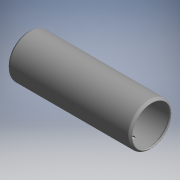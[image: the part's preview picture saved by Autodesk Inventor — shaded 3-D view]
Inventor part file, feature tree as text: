
AUTODESK INVENTOR PART (.ipt)
format: ipt  version: 2017.3 (Build 213256000, 256)  size: 147,456 bytes
history: native  units: mm (DEFAULTED — no unit token found)
features: other x42, sketch x2, revolve x1, extrude x1
ambient origin geometry x8: Origin, YZ Plane, XZ Plane, XY Plane, X Axis, Y Axis, Z Axis, Center Point
bodies: Solid1 (feature_tree)
feature tree (46):
  revolve  "Revolution1"  [1 undecoded]
  extrude  "Extrusion1"  [1 undecoded]
  other  "cp1_XY"
  other  "cp1_YZ"
  other  "cp1_ZX"
  other  "cp1_X"
  other  "cp1_Y"
  other  "cp1_Z"
  other  "cp1_Center"
  other  "cp2_XY"
  other  "cp2_YZ"
  other  "cp2_ZX"
  other  "cp2_X"
  other  "cp2_Y"
  other  "cp2_Z"
  other  "cp2_Center"
  other  "cp3_XY"
  other  "cp3_YZ"
  other  "cp3_ZX"
  other  "cp3_X"
  other  "cp3_Y"
  other  "cp3_Z"
  other  "cp3_Center"
  other  "cp4_XY"
  other  "cp4_YZ"
  other  "cp4_ZX"
  other  "cp4_X"
  other  "cp4_Y"
  other  "cp4_Z"
  other  "cp4_Center"
  other  "tube_front_XY"
  other  "tube_front_YZ"
  other  "tube_front_ZX"
  other  "tube_front_X"
  other  "tube_front_Y"
  other  "tube_front_Z"
  other  "tube_front_Center"
  other  "tube_rear_XY"
  other  "tube_rear_YZ"
  other  "tube_rear_ZX"
  other  "tube_rear_X"
  other  "tube_rear_Y"
  other  "tube_rear_Z"
  other  "tube_rear_Center"
  sketch  "Sketch_1"  dims[d0=360.0deg d1=10.2235mm d2=0.0mm]
  sketch  "Sketch_4"
note: 2 required parameter values undecoded (feature->parameter linkage not recoverable at this tier; creation-order binding heuristic only, values carry confidence <= 0.55)